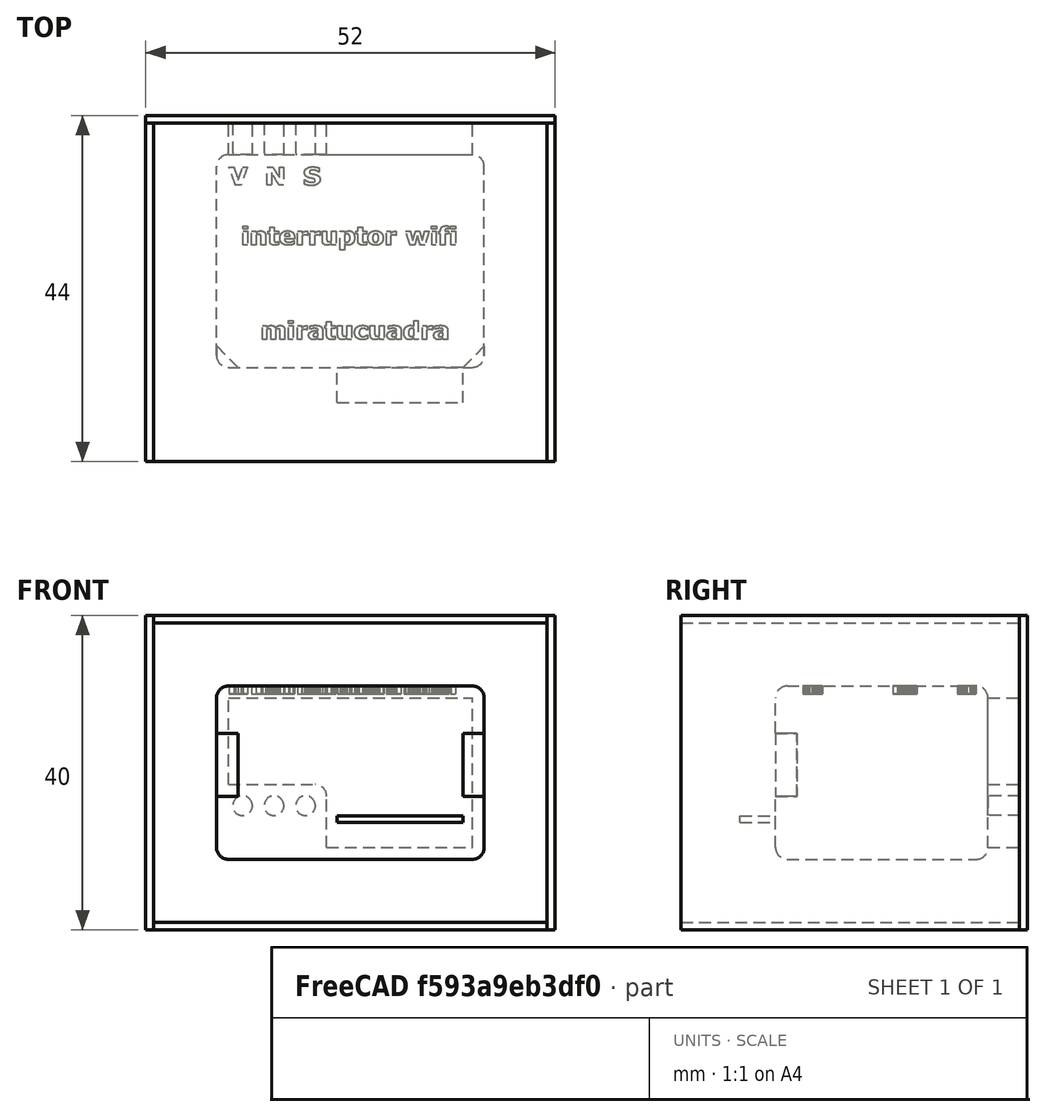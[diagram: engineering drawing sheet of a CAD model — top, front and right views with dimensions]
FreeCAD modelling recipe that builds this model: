
FCSTD DOCUMENT  (FreeCAD 0.20R29410 (Git))
Label: device01_molde
License: All rights reserved
LicenseURL: http://en.wikipedia.org/wiki/All_rights_reserved
objects: Part::Extrusion×65, Part::Feature×41, Part::Box×12, Part::Cut×12, Part::MultiFuse×5, Part::Cylinder×3, Part::Fillet×2, Part::Fuse×1
note: 141 computed .brp shape members not serialized (recipe doc carries the construction recipe); baked Part::Feature solids carry a one-line shape summary decoded from their .brp

FEATURE [Part::Box] Box010  label="fundaprisma"
  AttacherType = Attacher::AttachEngine3D
  Height = 22
  Length = 34
  Placement = pos=(-1.3,-1.5,-3) rot=(0,0,1;0rad)
  Width = 27
FEATURE [Part::Cylinder] Cylinder  label="vivo"
  Angle = 360
  AttacherType = Attacher::AttachEngine3D
  FirstAngle = 0
  Height = 6.5
  Placement = pos=(2,23,3.8) rot=(-1,0,0;1.5708rad)
  Radius = 1.25
  SecondAngle = 0
FEATURE [Part::Cylinder] Cylinder001  label="neutro"
  Angle = 360
  AttacherType = Attacher::AttachEngine3D
  FirstAngle = 0
  Height = 6.5
  Placement = pos=(6,23,3.8) rot=(-1,0,0;1.5708rad)
  Radius = 1.25
  SecondAngle = 0
FEATURE [Part::Cylinder] Cylinder002  label="salida"
  Angle = 360
  AttacherType = Attacher::AttachEngine3D
  FirstAngle = 0
  Height = 6.5
  Placement = pos=(10,23,3.8) rot=(-1,0,0;1.5708rad)
  Radius = 1.25
  SecondAngle = 0
FEATURE [Part::Box] Box019  label="apoyorele"
  AttacherType = Attacher::AttachEngine3D
  Height = 8
  Length = 2
  Placement = pos=(0.5,-3.4,5) rot=(0,0,1;0.785398rad)
  Width = 5
FEATURE [Part::Box] Box020  label="noapoyorele"
  AttacherType = Attacher::AttachEngine3D
  Height = 8
  Length = 2
  Placement = pos=(29.5,-2,5) rot=(0,0,-1;0.785398rad)
  Width = 5
FEATURE [Part::MultiFuse] Fusion002
  Shapes = -> [Box020,Box019]
FEATURE [Part::Cut] Cut
  Base = -> Box010
  Tool = -> Fusion002
FEATURE [Part::Fillet] Fillet  label="sinescribir"
  Base = -> Cut
  Edges = 14 edges r=1.5: [Edge1,Edge5,Edge6,Edge7,Edge8,Edge9,Edge13,Edge14,Edge18,Edge21,Edge22,Edge23,Edge24,Edge25]
FEATURE [Part::Box] Box021  label="Cubo"
  AttacherType = Attacher::AttachEngine3D
  Height = 19
  Length = 31
  Placement = pos=(0.2,25.5,-1.5) rot=(0,0,1;0rad)
  Width = 4
FEATURE [Part::Box] Box022  label="Cubo001"
  AttacherType = Attacher::AttachEngine3D
  Height = 8
  Length = 12.5
  Placement = pos=(0.2,25.5,-1.5) rot=(0,0,1;0rad)
  Width = 4
FEATURE [Part::Fillet] Fillet001
  Base = -> Box022
  Edges = 1 edges r=1.5: [Edge6]
FEATURE [Part::Cut] Cut001  label="paracolar"
  Base = -> Box021
  Tool = -> Fillet001
FEATURE [Part::Feature] path3990
  shape: bbox 2.35 x 2.308 x 2e-07 mm, 0 faces, 0 solids (baked)
FEATURE [Part::Extrusion] Extrude
  Base = -> path3990
  Dir = (0,0,-1)
  DirMode = 2
  FaceMakerClass = Part::FaceMakerBullseye
  LengthFwd = 1
  LengthRev = 0
  Solid = true
  Symmetric = false
FEATURE [Part::Feature] path3992
  shape: bbox 2.099 x 2.308 x 2e-07 mm, 0 faces, 0 solids (baked)
FEATURE [Part::Extrusion] Extrude001
  Base = -> path3992
  Dir = (0,0,-1)
  DirMode = 2
  FaceMakerClass = Part::FaceMakerBullseye
  LengthFwd = 1
  LengthRev = 0
  Solid = true
  Symmetric = false
FEATURE [Part::Feature] path3994
  shape: bbox 1.974 x 2.392 x 2e-07 mm, 0 faces, 0 solids (baked)
FEATURE [Part::Extrusion] Extrude002
  Base = -> path3994
  Dir = (0,0,-1)
  DirMode = 2
  FaceMakerClass = Part::FaceMakerBullseye
  LengthFwd = 1
  LengthRev = 0
  Solid = true
  Symmetric = false
FEATURE [Part::MultiFuse] Fusion003
  Placement = pos=(6,23,19) rot=(0,0,1;0rad)
  Shapes = -> [Extrude002,Extrude,Extrude001]
FEATURE [Part::Cut] Cut002
  Base = -> Fillet
  Tool = -> Fusion003
FEATURE [Part::Feature] path3995
  shape: bbox 0.5581 x 1.741 x 2e-07 mm, 0 faces, 0 solids (baked)
FEATURE [Part::Extrusion] Extrude003
  Base = -> path3995
  Dir = (0,0,-1)
  DirMode = 2
  FaceMakerClass = Part::FaceMakerBullseye
  LengthFwd = 1
  LengthRev = 0
  Solid = true
  Symmetric = false
FEATURE [Part::Extrusion] Extrude022
  Base = -> path3995
  Dir = (0,0,-1)
  DirMode = 2
  FaceMakerClass = Part::FaceMakerBullseye
  LengthFwd = 1
  LengthRev = 0
  Solid = true
  Symmetric = false
FEATURE [Part::Feature] path3990001
  shape: bbox 0.5891 x 0.4232 x 2e-07 mm, 0 faces, 0 solids (baked)
FEATURE [Part::Extrusion] Extrude004
  Base = -> path3990001
  Dir = (0,0,-1)
  DirMode = 2
  FaceMakerClass = Part::FaceMakerBullseye
  LengthFwd = 1
  LengthRev = 0
  Solid = true
  Symmetric = false
FEATURE [Part::Extrusion] Extrude023
  Base = -> path3990001
  Dir = (0,0,-1)
  DirMode = 2
  FaceMakerClass = Part::FaceMakerBullseye
  LengthFwd = 1
  LengthRev = 0
  Solid = true
  Symmetric = false
FEATURE [Part::Feature] path3990002
  shape: bbox 1.749 x 1.789 x 2e-07 mm, 0 faces, 0 solids (baked)
FEATURE [Part::Extrusion] Extrude005
  Base = -> path3990002
  Dir = (0,0,-1)
  DirMode = 2
  FaceMakerClass = Part::FaceMakerBullseye
  LengthFwd = 1
  LengthRev = 0
  Solid = true
  Symmetric = false
FEATURE [Part::Extrusion] Extrude024
  Base = -> path3990002
  Dir = (0,0,-1)
  DirMode = 2
  FaceMakerClass = Part::FaceMakerBullseye
  LengthFwd = 1
  LengthRev = 0
  Solid = true
  Symmetric = false
FEATURE [Part::Feature] path3990003
  shape: bbox 1.31 x 2.273 x 2e-07 mm, 0 faces, 0 solids (baked)
FEATURE [Part::Extrusion] Extrude006
  Base = -> path3990003
  Dir = (0,0,-1)
  DirMode = 2
  FaceMakerClass = Part::FaceMakerBullseye
  LengthFwd = 1
  LengthRev = 0
  Solid = true
  Symmetric = false
FEATURE [Part::Extrusion] Extrude025
  Base = -> path3990003
  Dir = (0,0,-1)
  DirMode = 2
  FaceMakerClass = Part::FaceMakerBullseye
  LengthFwd = 1
  LengthRev = 0
  Solid = true
  Symmetric = false
FEATURE [Part::Feature] path3996
  shape: bbox 1.842 x 1.842 x 2e-07 mm, 0 faces, 0 solids (baked)
FEATURE [Part::Extrusion] Extrude007
  Base = -> path3996
  Dir = (0,0,-1)
  DirMode = 2
  FaceMakerClass = Part::FaceMakerBullseye
  LengthFwd = 1
  LengthRev = 0
  Solid = true
  Symmetric = false
FEATURE [Part::Feature] path3996001
  shape: bbox 0.724 x 0.3519 x 2e-07 mm, 0 faces, 0 solids (baked)
FEATURE [Part::Extrusion] Extrude008
  Base = -> path3996001
  Dir = (0,0,1)
  DirMode = 2
  FaceMakerClass = Part::FaceMakerBullseye
  LengthFwd = 1
  LengthRev = 0
  Placement = pos=(0,0,-1) rot=(0,0,1;0rad)
  Solid = true
  Symmetric = false
FEATURE [Part::Cut] Cut003
  Base = -> Extrude007
  Tool = -> Extrude008
FEATURE [Part::Feature] path3998
  shape: bbox 1.262 x 1.747 x 2e-07 mm, 0 faces, 0 solids (baked)
FEATURE [Part::Extrusion] Extrude009
  Base = -> path3998
  Dir = (0,0,-1)
  DirMode = 2
  FaceMakerClass = Part::FaceMakerBullseye
  LengthFwd = 1
  LengthRev = 0
  Solid = true
  Symmetric = false
FEATURE [Part::Extrusion] Extrude027
  Base = -> path3998
  Dir = (0,0,-1)
  DirMode = 2
  FaceMakerClass = Part::FaceMakerBullseye
  LengthFwd = 1
  LengthRev = 0
  Solid = true
  Symmetric = false
FEATURE [Part::Feature] path4000
  shape: bbox 1.262 x 1.747 x 2e-07 mm, 0 faces, 0 solids (baked)
FEATURE [Part::Extrusion] Extrude010
  Base = -> path4000
  Dir = (0,0,-1)
  DirMode = 2
  FaceMakerClass = Part::FaceMakerBullseye
  LengthFwd = 1
  LengthRev = 0
  Solid = true
  Symmetric = false
FEATURE [Part::Extrusion] Extrude028
  Base = -> path4000
  Dir = (0,0,-1)
  DirMode = 2
  FaceMakerClass = Part::FaceMakerBullseye
  LengthFwd = 1
  LengthRev = 0
  Solid = true
  Symmetric = false
FEATURE [Part::Feature] path4002
  shape: bbox 1.749 x 1.789 x 2e-07 mm, 0 faces, 0 solids (baked)
FEATURE [Part::Extrusion] Extrude011
  Base = -> path4002
  Dir = (0,0,-1)
  DirMode = 2
  FaceMakerClass = Part::FaceMakerBullseye
  LengthFwd = 1
  LengthRev = 0
  Solid = true
  Symmetric = false
FEATURE [Part::Extrusion] Extrude029
  Base = -> path4002
  Dir = (0,0,-1)
  DirMode = 2
  FaceMakerClass = Part::FaceMakerBullseye
  LengthFwd = 1
  LengthRev = 0
  Solid = true
  Symmetric = false
FEATURE [Part::Feature] path4004
  shape: bbox 1.817 x 2.428 x 2e-07 mm, 0 faces, 0 solids (baked)
FEATURE [Part::Extrusion] Extrude030
  Base = -> path4004
  Dir = (0,0,-1)
  DirMode = 2
  FaceMakerClass = Part::FaceMakerBullseye
  LengthFwd = 1
  LengthRev = 0
  Solid = true
  Symmetric = false
FEATURE [Part::Feature] path4004001
  shape: bbox 0.6837 x 1.003 x 2e-07 mm, 0 faces, 0 solids (baked)
FEATURE [Part::Extrusion] Extrude031
  Base = -> path4004001
  Dir = (0,0,1)
  DirMode = 2
  FaceMakerClass = Part::FaceMakerBullseye
  LengthFwd = 1
  LengthRev = 0
  Placement = pos=(0,0,-1) rot=(0,0,1;0rad)
  Solid = true
  Symmetric = false
FEATURE [Part::Cut] Cut004
  Base = -> Extrude030
  Tool = -> Extrude031
FEATURE [Part::Feature] path4006
  shape: bbox 1.31 x 2.273 x 2e-07 mm, 0 faces, 0 solids (baked)
FEATURE [Part::Extrusion] Extrude012
  Base = -> path4006
  Dir = (0,0,-1)
  DirMode = 2
  FaceMakerClass = Part::FaceMakerBullseye
  LengthFwd = 1
  LengthRev = 0
  Solid = true
  Symmetric = false
FEATURE [Part::Extrusion] Extrude032
  Base = -> path4006
  Dir = (0,0,-1)
  DirMode = 2
  FaceMakerClass = Part::FaceMakerBullseye
  LengthFwd = 1
  LengthRev = 0
  Solid = true
  Symmetric = false
FEATURE [Part::Feature] path4008
  shape: bbox 1.907 x 1.849 x 2e-07 mm, 0 faces, 0 solids (baked)
FEATURE [Part::Extrusion] Extrude013
  Base = -> path4008
  Dir = (0,0,-1)
  DirMode = 2
  FaceMakerClass = Part::FaceMakerBullseye
  LengthFwd = 1
  LengthRev = 0
  Solid = true
  Symmetric = false
FEATURE [Part::Feature] path4008001
  shape: bbox 0.7503 x 1.071 x 2e-07 mm, 0 faces, 0 solids (baked)
FEATURE [Part::Extrusion] Extrude014
  Base = -> path4008001
  Dir = (0,0,1)
  DirMode = 2
  FaceMakerClass = Part::FaceMakerBullseye
  LengthFwd = 1
  LengthRev = 0
  Placement = pos=(0,0,-1) rot=(0,0,1;0rad)
  Solid = true
  Symmetric = false
FEATURE [Part::Cut] Cut005
  Base = -> Extrude013
  Tool = -> Extrude014
FEATURE [Part::Feature] path4010
  shape: bbox 1.262 x 1.747 x 2e-07 mm, 0 faces, 0 solids (baked)
FEATURE [Part::Extrusion] Extrude015
  Base = -> path4010
  Dir = (0,0,-1)
  DirMode = 2
  FaceMakerClass = Part::FaceMakerBullseye
  LengthFwd = 1
  LengthRev = 0
  Solid = true
  Symmetric = false
FEATURE [Part::Extrusion] Extrude035
  Base = -> path4010
  Dir = (0,0,-1)
  DirMode = 2
  FaceMakerClass = Part::FaceMakerBullseye
  LengthFwd = 1
  LengthRev = 0
  Solid = true
  Symmetric = false
FEATURE [Part::Feature] path4012
  shape: bbox 2.97 x 1.741 x 2e-07 mm, 0 faces, 0 solids (baked)
FEATURE [Part::Extrusion] Extrude016
  Base = -> path4012
  Dir = (0,0,-1)
  DirMode = 2
  FaceMakerClass = Part::FaceMakerBullseye
  LengthFwd = 1
  LengthRev = 0
  Solid = true
  Symmetric = false
FEATURE [Part::Extrusion] Extrude036
  Base = -> path4012
  Dir = (0,0,-1)
  DirMode = 2
  FaceMakerClass = Part::FaceMakerBullseye
  LengthFwd = 1
  LengthRev = 0
  Solid = true
  Symmetric = false
FEATURE [Part::Feature] path4014
  shape: bbox 0.5581 x 1.741 x 2e-07 mm, 0 faces, 0 solids (baked)
FEATURE [Part::Extrusion] Extrude017
  Base = -> path4014
  Dir = (0,0,-1)
  DirMode = 2
  FaceMakerClass = Part::FaceMakerBullseye
  LengthFwd = 1
  LengthRev = 0
  Solid = true
  Symmetric = false
FEATURE [Part::Extrusion] Extrude037
  Base = -> path4014
  Dir = (0,0,-1)
  DirMode = 2
  FaceMakerClass = Part::FaceMakerBullseye
  LengthFwd = 1
  LengthRev = 0
  Solid = true
  Symmetric = false
FEATURE [Part::Feature] path4014001
  shape: bbox 0.5891 x 0.4232 x 2e-07 mm, 0 faces, 0 solids (baked)
FEATURE [Part::Extrusion] Extrude018
  Base = -> path4014001
  Dir = (0,0,-1)
  DirMode = 2
  FaceMakerClass = Part::FaceMakerBullseye
  LengthFwd = 1
  LengthRev = 0
  Solid = true
  Symmetric = false
FEATURE [Part::Extrusion] Extrude038
  Base = -> path4014001
  Dir = (0,0,-1)
  DirMode = 2
  FaceMakerClass = Part::FaceMakerBullseye
  LengthFwd = 1
  LengthRev = 0
  Solid = true
  Symmetric = false
FEATURE [Part::Feature] path4016
  shape: bbox 1.326 x 2.428 x 2e-07 mm, 0 faces, 0 solids (baked)
FEATURE [Part::Extrusion] Extrude019
  Base = -> path4016
  Dir = (0,0,-1)
  DirMode = 2
  FaceMakerClass = Part::FaceMakerBullseye
  LengthFwd = 1
  LengthRev = 0
  Solid = true
  Symmetric = false
FEATURE [Part::Extrusion] Extrude039
  Base = -> path4016
  Dir = (0,0,-1)
  DirMode = 2
  FaceMakerClass = Part::FaceMakerBullseye
  LengthFwd = 1
  LengthRev = 0
  Solid = true
  Symmetric = false
FEATURE [Part::Feature] path4018
  shape: bbox 0.5581 x 1.741 x 2e-07 mm, 0 faces, 0 solids (baked)
FEATURE [Part::Extrusion] Extrude020
  Base = -> path4018
  Dir = (0,0,-1)
  DirMode = 2
  FaceMakerClass = Part::FaceMakerBullseye
  LengthFwd = 1
  LengthRev = 0
  Solid = true
  Symmetric = false
FEATURE [Part::Extrusion] Extrude040
  Base = -> path4018
  Dir = (0,0,-1)
  DirMode = 2
  FaceMakerClass = Part::FaceMakerBullseye
  LengthFwd = 1
  LengthRev = 0
  Solid = true
  Symmetric = false
FEATURE [Part::Feature] path4018001
  shape: bbox 0.5891 x 0.4232 x 2e-07 mm, 0 faces, 0 solids (baked)
FEATURE [Part::Extrusion] Extrude021
  Base = -> path4018001
  Dir = (0,0,-1)
  DirMode = 2
  FaceMakerClass = Part::FaceMakerBullseye
  LengthFwd = 1
  LengthRev = 0
  Solid = true
  Symmetric = false
FEATURE [Part::Extrusion] Extrude041
  Base = -> path4018001
  Dir = (0,0,-1)
  DirMode = 2
  FaceMakerClass = Part::FaceMakerBullseye
  LengthFwd = 1
  LengthRev = 0
  Solid = true
  Symmetric = false
FEATURE [Part::MultiFuse] Fusion004
  Placement = pos=(9,15,19) rot=(0,0,1;0rad)
  Shapes = -> [Extrude003,Extrude004,Extrude005,Extrude006,Extrude009,Extrude010,Extrude011,Extrude012,Extrude015,Extrude016,Extrude017,Extrude018,Extrude019,Extrude020,Extrude021,Extrude022,Extrude023,Extrude024,Extrude025,Extrude027,Extrude028,Extrude029,Extrude032,Extrude035,Extrude036,Extrude037,Extrude038,Extrude039,Extrude040,Extrude041,Cut003,Cut004,Cut005]
FEATURE [Part::Cut] Cut006
  Base = -> Cut002
  Tool = -> Fusion004
FEATURE [Part::Feature] path3717
  shape: bbox 2.846 x 1.789 x 2e-07 mm, 0 faces, 0 solids (baked)
FEATURE [Part::Extrusion] Extrude042
  Base = -> path3717
  Dir = (0,0,-1)
  DirMode = 2
  FaceMakerClass = Part::FaceMakerBullseye
  LengthFwd = 1
  LengthRev = 0
  Solid = true
  Symmetric = false
FEATURE [Part::Extrusion] Extrude059
  Base = -> path3717
  Dir = (0,0,-1)
  DirMode = 2
  FaceMakerClass = Part::FaceMakerBullseye
  LengthFwd = 1
  LengthRev = 0
  Solid = true
  Symmetric = false
FEATURE [Part::Feature] path3719
  shape: bbox 0.5581 x 1.741 x 2e-07 mm, 0 faces, 0 solids (baked)
FEATURE [Part::Extrusion] Extrude043
  Base = -> path3719
  Dir = (0,0,-1)
  DirMode = 2
  FaceMakerClass = Part::FaceMakerBullseye
  LengthFwd = 1
  LengthRev = 0
  Solid = true
  Symmetric = false
FEATURE [Part::Extrusion] Extrude060
  Base = -> path3719
  Dir = (0,0,-1)
  DirMode = 2
  FaceMakerClass = Part::FaceMakerBullseye
  LengthFwd = 1
  LengthRev = 0
  Solid = true
  Symmetric = false
FEATURE [Part::Feature] path3719001
  shape: bbox 0.5891 x 0.4232 x 2e-07 mm, 0 faces, 0 solids (baked)
FEATURE [Part::Extrusion] Extrude044
  Base = -> path3719001
  Dir = (0,0,-1)
  DirMode = 2
  FaceMakerClass = Part::FaceMakerBullseye
  LengthFwd = 1
  LengthRev = 0
  Solid = true
  Symmetric = false
FEATURE [Part::Extrusion] Extrude061
  Base = -> path3719001
  Dir = (0,0,-1)
  DirMode = 2
  FaceMakerClass = Part::FaceMakerBullseye
  LengthFwd = 1
  LengthRev = 0
  Solid = true
  Symmetric = false
FEATURE [Part::Feature] path3721
  shape: bbox 1.262 x 1.747 x 2e-07 mm, 0 faces, 0 solids (baked)
FEATURE [Part::Extrusion] Extrude045
  Base = -> path3721
  Dir = (0,0,-1)
  DirMode = 2
  FaceMakerClass = Part::FaceMakerBullseye
  LengthFwd = 1
  LengthRev = 0
  Solid = true
  Symmetric = false
FEATURE [Part::Extrusion] Extrude062
  Base = -> path3721
  Dir = (0,0,-1)
  DirMode = 2
  FaceMakerClass = Part::FaceMakerBullseye
  LengthFwd = 1
  LengthRev = 0
  Solid = true
  Symmetric = false
FEATURE [Part::Feature] path3723
  shape: bbox 0.617 x 0.4868 x 2e-07 mm, 0 faces, 0 solids (baked)
FEATURE [Part::Extrusion] Extrude046
  Base = -> path3723
  Dir = (0,0,1)
  DirMode = 2
  FaceMakerClass = Part::FaceMakerBullseye
  LengthFwd = 1
  LengthRev = 0
  Placement = pos=(0,0,-1) rot=(0,0,1;0rad)
  Solid = true
  Symmetric = false
FEATURE [Part::Feature] path3723001
  shape: bbox 1.738 x 1.837 x 2e-07 mm, 0 faces, 0 solids (baked)
FEATURE [Part::Extrusion] Extrude047
  Base = -> path3723001
  Dir = (0,0,-1)
  DirMode = 2
  FaceMakerClass = Part::FaceMakerBullseye
  LengthFwd = 1
  LengthRev = 0
  Solid = true
  Symmetric = false
FEATURE [Part::Cut] Cut007
  Base = -> Extrude047
  Tool = -> Extrude046
FEATURE [Part::Feature] path3725
  shape: bbox 1.31 x 2.273 x 2e-07 mm, 0 faces, 0 solids (baked)
FEATURE [Part::Extrusion] Extrude048
  Base = -> path3725
  Dir = (0,0,-1)
  DirMode = 2
  FaceMakerClass = Part::FaceMakerBullseye
  LengthFwd = 1
  LengthRev = 0
  Solid = true
  Symmetric = false
FEATURE [Part::Extrusion] Extrude063
  Base = -> path3725
  Dir = (0,0,-1)
  DirMode = 2
  FaceMakerClass = Part::FaceMakerBullseye
  LengthFwd = 1
  LengthRev = 0
  Solid = true
  Symmetric = false
FEATURE [Part::Feature] path3727
  shape: bbox 1.749 x 1.789 x 2e-07 mm, 0 faces, 0 solids (baked)
FEATURE [Part::Extrusion] Extrude049
  Base = -> path3727
  Dir = (0,0,-1)
  DirMode = 2
  FaceMakerClass = Part::FaceMakerBullseye
  LengthFwd = 1
  LengthRev = 0
  Solid = true
  Symmetric = false
FEATURE [Part::Extrusion] Extrude064
  Base = -> path3727
  Dir = (0,0,-1)
  DirMode = 2
  FaceMakerClass = Part::FaceMakerBullseye
  LengthFwd = 1
  LengthRev = 0
  Solid = true
  Symmetric = false
FEATURE [Part::Feature] path3729
  shape: bbox 1.626 x 1.836 x 2e-07 mm, 0 faces, 0 solids (baked)
FEATURE [Part::Extrusion] Extrude050
  Base = -> path3729
  Dir = (0,0,-1)
  DirMode = 2
  FaceMakerClass = Part::FaceMakerBullseye
  LengthFwd = 1
  LengthRev = 0
  Solid = true
  Symmetric = false
FEATURE [Part::Extrusion] Extrude065
  Base = -> path3729
  Dir = (0,0,-1)
  DirMode = 2
  FaceMakerClass = Part::FaceMakerBullseye
  LengthFwd = 1
  LengthRev = 0
  Solid = true
  Symmetric = false
FEATURE [Part::Feature] path3731
  shape: bbox 1.749 x 1.789 x 2e-07 mm, 0 faces, 0 solids (baked)
FEATURE [Part::Extrusion] Extrude051
  Base = -> path3731
  Dir = (0,0,-1)
  DirMode = 2
  FaceMakerClass = Part::FaceMakerBullseye
  LengthFwd = 1
  LengthRev = 0
  Solid = true
  Symmetric = false
FEATURE [Part::Extrusion] Extrude026
  Base = -> path3731
  Dir = (0,0,-1)
  DirMode = 2
  FaceMakerClass = Part::FaceMakerBullseye
  LengthFwd = 1
  LengthRev = 0
  Solid = true
  Symmetric = false
FEATURE [Part::Feature] path3733
  shape: bbox 0.617 x 0.4868 x 2e-07 mm, 0 faces, 0 solids (baked)
FEATURE [Part::Extrusion] Extrude052
  Base = -> path3733
  Dir = (0,0,1)
  DirMode = 2
  FaceMakerClass = Part::FaceMakerBullseye
  LengthFwd = 1
  LengthRev = 0
  Placement = pos=(0,0,-1) rot=(0,0,1;0rad)
  Solid = true
  Symmetric = false
FEATURE [Part::Feature] path3733001
  shape: bbox 1.738 x 1.837 x 2e-07 mm, 0 faces, 0 solids (baked)
FEATURE [Part::Extrusion] Extrude053
  Base = -> path3733001
  Dir = (0,0,-1)
  DirMode = 2
  FaceMakerClass = Part::FaceMakerBullseye
  LengthFwd = 1
  LengthRev = 0
  Solid = true
  Symmetric = false
FEATURE [Part::Cut] Cut008
  Base = -> Extrude053
  Tool = -> Extrude052
FEATURE [Part::Feature] path3735
  shape: bbox 1.817 x 2.46 x 2e-07 mm, 0 faces, 0 solids (baked)
FEATURE [Part::Extrusion] Extrude054
  Base = -> path3735
  Dir = (0,0,-1)
  DirMode = 2
  FaceMakerClass = Part::FaceMakerBullseye
  LengthFwd = 1
  LengthRev = 0
  Solid = true
  Symmetric = false
FEATURE [Part::Feature] path3735001
  shape: bbox 0.6837 x 1.005 x 2e-07 mm, 0 faces, 0 solids (baked)
FEATURE [Part::Extrusion] Extrude055
  Base = -> path3735001
  Dir = (0,0,1)
  DirMode = 2
  FaceMakerClass = Part::FaceMakerBullseye
  LengthFwd = 1
  LengthRev = 0
  Placement = pos=(0,0,-1) rot=(0,0,1;0rad)
  Solid = true
  Symmetric = false
FEATURE [Part::Cut] Cut009
  Base = -> Extrude054
  Tool = -> Extrude055
FEATURE [Part::Feature] path3737
  shape: bbox 1.262 x 1.747 x 2e-07 mm, 0 faces, 0 solids (baked)
FEATURE [Part::Extrusion] Extrude056
  Base = -> path3737
  Dir = (0,0,-1)
  DirMode = 2
  FaceMakerClass = Part::FaceMakerBullseye
  LengthFwd = 1
  LengthRev = 0
  Solid = true
  Symmetric = false
FEATURE [Part::Extrusion] Extrude066
  Base = -> path3737
  Dir = (0,0,-1)
  DirMode = 2
  FaceMakerClass = Part::FaceMakerBullseye
  LengthFwd = 1
  LengthRev = 0
  Solid = true
  Symmetric = false
FEATURE [Part::Feature] path3739
  shape: bbox 0.617 x 0.4868 x 2e-07 mm, 0 faces, 0 solids (baked)
FEATURE [Part::Extrusion] Extrude057
  Base = -> path3739
  Dir = (0,0,1)
  DirMode = 2
  FaceMakerClass = Part::FaceMakerBullseye
  LengthFwd = 1
  LengthRev = 0
  Placement = pos=(0,0,-1) rot=(0,0,1;0rad)
  Solid = true
  Symmetric = false
FEATURE [Part::Feature] path3739001
  shape: bbox 1.738 x 1.837 x 2e-07 mm, 0 faces, 0 solids (baked)
FEATURE [Part::Extrusion] Extrude058
  Base = -> path3739001
  Dir = (0,0,-1)
  DirMode = 2
  FaceMakerClass = Part::FaceMakerBullseye
  LengthFwd = 1
  LengthRev = 0
  Solid = true
  Symmetric = false
FEATURE [Part::Cut] Cut010
  Base = -> Extrude058
  Tool = -> Extrude057
FEATURE [Part::MultiFuse] Fusion005
  Placement = pos=(15,3,19) rot=(0,0,1;0rad)
  Shapes = -> [Extrude042,Extrude043,Extrude044,Extrude045,Extrude048,Extrude049,Extrude050,Extrude051,Extrude056,Extrude059,Extrude060,Extrude061,Extrude062,Extrude063,Extrude064,Extrude065,Extrude026,Extrude066,Cut007,Cut008,Cut009,Cut010]
FEATURE [Part::Cut] Cut011  label="funda"
  Base = -> Cut006
  Tool = -> Fusion005
FEATURE [Part::Box] Box013  label="base8267"
  AttacherType = Attacher::AttachEngine3D
  Height = 2.3
  Length = 12
  Placement = pos=(16,1.5,1.7) rot=(0,0,1;0rad)
  Width = 15
FEATURE [Part::Box] Box012  label="base8266"
  AttacherType = Attacher::AttachEngine3D
  Height = 0.8
  Length = 16
  Placement = pos=(14,-6,1.7) rot=(0,0,1;0rad)
  Width = 24
FEATURE [Part::Fuse] Fusion  label="8266"
  Base = -> Box012
  Tool = -> Box013
FEATURE [Part::MultiFuse] Fusion006  label="molde"
  Shapes = -> [Fusion,Cylinder,Cylinder001,Cylinder002,Cut001,Cut011]
FEATURE [Part::Box] Box  label="base"
  AttacherType = Attacher::AttachEngine3D
  Height = 40
  Length = 52
  Placement = pos=(-10.3,29.5,-12) rot=(0,0,1;0rad)
  Width = 1
FEATURE [Part::Box] Box023  label="frente"
  AttacherType = Attacher::AttachEngine3D
  Height = 1
  Length = 50
  Placement = pos=(-9.3,-13.5,27) rot=(0,0,1;0rad)
  Width = 43
FEATURE [Part::Box] Box024  label="derecha"
  AttacherType = Attacher::AttachEngine3D
  Height = 40
  Length = 43
  Placement = pos=(-9.3,-13.5,-12) rot=(0,0,1;1.5708rad)
  Width = 1
FEATURE [Part::Box] Box025  label="atras"
  AttacherType = Attacher::AttachEngine3D
  Height = 1
  Length = 50
  Placement = pos=(-9.3,-13.5,-12) rot=(0,0,1;0rad)
  Width = 43
FEATURE [Part::Box] Box026  label="izquierda"
  AttacherType = Attacher::AttachEngine3D
  Height = 40
  Length = 43
  Placement = pos=(41.7,-13.5,-12) rot=(0,0,1;1.5708rad)
  Width = 1
